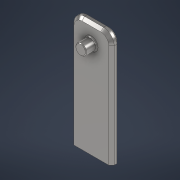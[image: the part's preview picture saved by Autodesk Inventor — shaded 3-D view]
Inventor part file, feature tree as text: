
AUTODESK INVENTOR PART (.ipt)
format: ipt  version: 2021 (Build 250183000, 183)  size: 280,064 bytes
history: native  units: mm
features: extrude x2, fillet x2, chamfer x2, sketch x2
ambient origin geometry x8: Origin, YZ Plane, XZ Plane, XY Plane, X Axis, Y Axis, Z Axis, Center Point
bodies: Solid1 (feature_tree)
feature tree (8):
  extrude  "Extrusion1"  Depth=85.0mm
  fillet  "Fillet1"  Radius=15.0mm
  extrude  "Extrusion2"  Depth=6.0mm TaperAngle=0.0deg
  fillet  "Fillet2"  Radius=8.0mm
  chamfer  "Chamfer1"  Distance=72.0mm
  chamfer  "Chamfer2"  Distance=8.0mm
  sketch  "Sketch1"  dims[d0=30.0mm d1=85.0mm d2=15.0mm]
  sketch  "Sketch2"  dims[d3=85.0mm d4=6.0mm d5=0.0mm d6=8.0mm d7=72.0mm d8=8.0mm d9=8.0mm d10=0.0mm d11=1.0mm d12=0.0mm d13=0.5mm d14=2.0mm d15=45.0deg d16=2.0mm d17=2.0mm d18=45.0deg]
